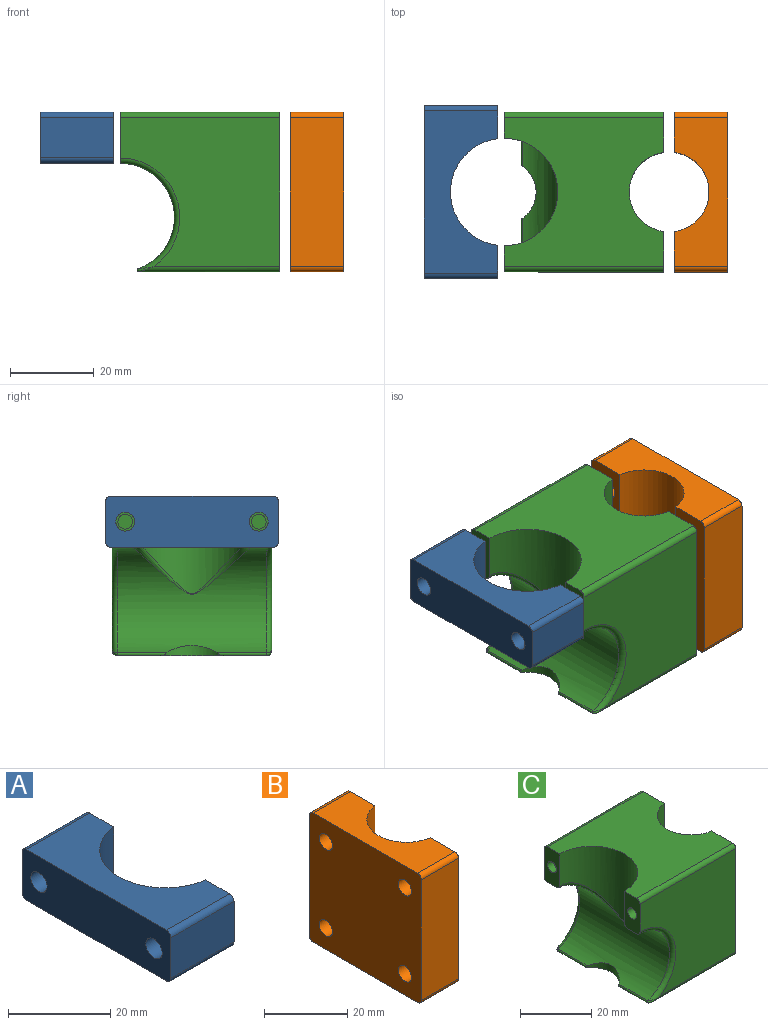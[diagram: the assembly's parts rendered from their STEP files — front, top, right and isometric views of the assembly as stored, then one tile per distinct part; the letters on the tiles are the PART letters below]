
ASSEMBLY  parts=3 mates=5
PART A: 14 faces, bbox 17.5x41.3x12.2 mm
  f0: plane 38.74x17.46mm, normal (0,0,-1), area 458.6mm2, adj f2,f5,f6,f7,f11,f12
  f1: plane 38.74x17.46mm, normal (0,0,1), area 458.6mm2, adj f2,f5,f6,f7,f10,f13
  f2: cylinder r=12.83mm len=25.46mm, axis (0,0,1), area 452.5mm2, adj f0,f1,f6,f7
  f3: cylinder r=2.25mm len=17.46mm, axis (-1,0,0), area 246.9mm2, adj f5,f7
  f4: cylinder r=2.25mm len=17.46mm, axis (-1,0,0), area 246.9mm2, adj f5,f6
  f5: plane 41.28x12.19mm, normal (-1,0,0), area 470mm2, adj f0,f1,f3,f4,f8,f9,f10,f11
  f6: plane 12.19x7.91mm, normal (1,0,0), area 79.8mm2, adj f0,f1,f2,f4,f9,f10,f11
  f7: plane 12.19x7.91mm, normal (1,0,0), area 79.8mm2, adj f0,f1,f2,f3,f8,f12,f13
  f8: plane 17.46x9.65mm, normal (0,1,0), area 168.5mm2, adj f5,f7,f12,f13
  f9: plane 17.46x9.65mm, normal (0,-1,0), area 168.5mm2, adj f5,f6,f10,f11
  f10: cylinder r=1.27mm len=17.46mm, axis (1,0,0), area 34.8mm2, adj f1,f5,f6,f9
  f11: cylinder r=1.27mm len=17.46mm, axis (-1,0,0), area 34.8mm2, adj f0,f5,f6,f9
  f12: cylinder r=1.27mm len=17.46mm, axis (-1,0,0), area 34.8mm2, adj f0,f5,f7,f8
  f13: cylinder r=1.27mm len=17.46mm, axis (1,0,0), area 34.8mm2, adj f1,f5,f7,f8
PART B: 16 faces, bbox 12.7x38.1x38.1 mm
  f0: plane 35.56x12.7mm, normal (0,0,1), area 333.2mm2, adj f1,f5,f6,f11,f13,f14
  f1: plane 38.1x9.61mm, normal (1,0,0), area 333.6mm2, adj f0,f2,f3,f7,f10,f11,f12,f13
  f2: plane 35.56x12.7mm, normal (0,0,-1), area 333.2mm2, adj f1,f5,f6,f11,f12,f15
  f3: plane 35.56x12.7mm, normal (0,1,0), area 451.6mm2, adj f1,f6,f12,f13
  f4: plane 35.56x12.7mm, normal (0,-1,0), area 451.6mm2, adj f5,f6,f14,f15
  f5: plane 38.1x9.61mm, normal (1,0,0), area 333.6mm2, adj f0,f2,f4,f8,f9,f11,f14,f15
  f6: plane 38.1x38.1mm, normal (-1,0,0), area 1386.6mm2, adj f0,f2,f3,f4,f7,f8,f9,f10
  f7: cylinder r=2.25mm len=12.7mm, axis (1,0,0), area 179.5mm2, adj f1,f6
  f8: cylinder r=2.25mm len=12.7mm, axis (1,0,0), area 179.5mm2, adj f5,f6
  f9: cylinder r=2.25mm len=12.7mm, axis (1,0,0), area 179.5mm2, adj f5,f6
  f10: cylinder r=2.25mm len=12.7mm, axis (1,0,0), area 179.5mm2, adj f1,f6
  f11: cylinder r=9.53mm len=38.1mm, axis (0,0,1), area 1043mm2, adj f0,f1,f2,f5
  f12: cylinder r=1.27mm len=12.7mm, axis (-1,0,0), area 25.3mm2, adj f1,f2,f3,f6
  f13: cylinder r=1.27mm len=12.7mm, axis (-1,0,0), area 25.3mm2, adj f0,f1,f3,f6
  f14: cylinder r=1.27mm len=12.7mm, axis (-1,0,0), area 25.3mm2, adj f0,f4,f5,f6
  f15: cylinder r=1.27mm len=12.7mm, axis (-1,0,0), area 25.3mm2, adj f2,f4,f5,f6
PART C: 35 faces, bbox 39.7x38.3x40.6 mm
  f0: plane 38.1x35.56mm, normal (0,0,1), area 978mm2, adj f1,f2,f6,f15,f17,f31,f32,f34
  f1: plane 12.23x6.26mm, normal (-1,0,0), area 65.2mm2, adj f0,f5,f16,f17,f23,f30,f31,f33
  f2: plane 38.1x9.61mm, normal (1,0,0), area 346.2mm2, adj f0,f3,f4,f7,f10,f25,f32,f34
  f3: plane 35.56x33.66mm, normal (0,0,-1), area 1050.9mm2, adj f2,f6,f18,f19,f20,f25,f28,f34
  f4: plane 38.1x35.56mm, normal (0,1,0), area 1051mm2, adj f2,f15,f25,f27,f32
  f5: plane 38.1x35.56mm, normal (0,-1,0), area 1051mm2, adj f1,f6,f28,f30,f31
  f6: plane 38.1x9.61mm, normal (1,0,0), area 346.2mm2, adj f0,f3,f5,f8,f9,f28,f31,f34
  f7: cylinder r=1.75mm len=12.7mm, axis (1,0,0), area 139.6mm2, adj f2,f14
  f8: cylinder r=1.75mm len=12.7mm, axis (1,0,0), area 139.6mm2, adj f6,f13
  f9: cylinder r=1.75mm len=12.7mm, axis (1,0,0), area 139.6mm2, adj f6,f12
  f10: cylinder r=1.75mm len=12.7mm, axis (1,0,0), area 139.6mm2, adj f2,f11
  f11: plane 3.5x3.5mm, normal (1,0,0), area 9.6mm2, adj f10
  f12: plane 3.5x3.5mm, normal (1,0,0), area 9.6mm2, adj f9
  f13: plane 3.5x3.5mm, normal (1,0,0), area 9.6mm2, adj f8
  f14: plane 3.5x3.5mm, normal (1,0,0), area 9.6mm2, adj f7
  f15: plane 12.23x6.26mm, normal (-1,0,0), area 65.2mm2, adj f0,f4,f16,f17,f21,f27,f32,f33
  f16: cylinder r=12.95mm len=35.56mm, axis (0,-1,0), area 902.4mm2, adj f1,f15,f18,f19,f20,f27,f30,f33
  f17: cylinder r=12.83mm len=25.65mm, axis (0,0,1), area 638.9mm2, adj f0,f1,f15,f33
  f18: cylinder r=7.62mm len=12.89mm, axis (0,0,-1), area 26.8mm2, adj f3,f16,f19,f20
  f19: cylinder r=0.38mm len=11.59mm, axis (0,-1,0), area 12.2mm2, adj f3,f16,f18,f29
  f20: cylinder r=0.38mm len=11.59mm, axis (0,-1,0), area 12.2mm2, adj f3,f16,f18,f26
  f21: cylinder r=1.75mm len=12.7mm, axis (-1,0,0), area 139.6mm2, adj f15,f22
  f22: plane 3.5x3.5mm, normal (-1,0,0), area 9.6mm2, adj f21
  f23: cylinder r=1.75mm len=12.7mm, axis (-1,0,0), area 139.6mm2, adj f1,f24
  f24: plane 3.5x3.5mm, normal (-1,0,0), area 9.6mm2, adj f23
  f25: cylinder r=1.27mm len=33.66mm, axis (-1,0,0), area 64.2mm2, adj f2,f3,f4,f26
  f26: bspline ~5.89x1.59mm, area 2.3mm2, adj f20,f25,f27
  f27: torus R=14.22mm, axis (0,-1,0), area 72mm2, adj f4,f15,f16,f26
  f28: cylinder r=1.27mm len=33.66mm, axis (-1,0,0), area 64.2mm2, adj f3,f5,f6,f29
  f29: bspline ~5.89x1.59mm, area 2.3mm2, adj f19,f28,f30
  f30: torus R=14.22mm, axis (0,1,0), area 72mm2, adj f1,f5,f16,f29
  f31: cylinder r=1.27mm len=38.1mm, axis (-1,0,0), area 76mm2, adj f0,f1,f5,f6
  f32: cylinder r=1.27mm len=38.1mm, axis (-1,0,0), area 76mm2, adj f0,f2,f4,f15
  f33: bspline ~28.22x14.38mm, area 57.1mm2, adj f1,f15,f16,f17
  f34: cylinder r=9.53mm len=38.1mm, axis (0,0,1), area 1043mm2, adj f0,f2,f3,f6
PLACE A t=(-21.36,39.84,24.11)mm
PLACE B rot(axis=(0,0,1),180deg) t=(51.03,39.84,-1.8)mm
PLACE C t=(23.09,1.74,-1.8)mm fixed
MATE parallel C.f32 <-> B.f5  axis (1,0,0) through (35.79,38.57,35.03)mm
MATE planar C.f0 <-> B.f0  axis (0,0,1) through (18.45,20.79,36.3)mm
MATE planar A.f1 <-> C.f0  axis (0,0,1) through (-14.53,20.79,36.3)mm
MATE cylindrical B.f11 <-> C.f34  axis (0,0,1) through (37.06,20.79,36.3)mm
MATE cylindrical C.f17 <-> A.f2  axis (0,0,1) through (-2.31,20.79,36.3)mm
